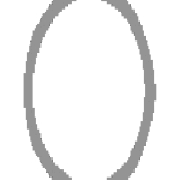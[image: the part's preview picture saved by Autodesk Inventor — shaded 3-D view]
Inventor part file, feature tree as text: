
AUTODESK INVENTOR PART (.ipt)
format: ipt  version: 2021 (Build 250183000, 183)  size: 110,080 bytes
history: native  units: in
note: dims shown in document units (in); Inventor stores cm internally (conversion verified against a paired STEP export)
features: other x4, sketch x3, plane x1
ambient origin geometry x8: Origin, YZ Plane, XZ Plane, XY Plane, X Axis, Y Axis, Z Axis, Center Point
bodies: Solid1 (feature_tree), Body (feature_tree)
feature tree (8):
  other  "Driven Length"
  other  "Frame Generator"
  other  "Start Plane"
  other  "End Plane"
  sketch  "Sketch"  dims[d2=14.4605in d4=-0.0in d5=14.4605in d6=0.12in d7=0.0in d8=90.0deg d9=14.4605in]
  sketch  "Sketch2"  dims[d0=1.0in]
  plane  "Work Plane3"
  sketch  "Sketch3"  dims[d1=0.065in]
